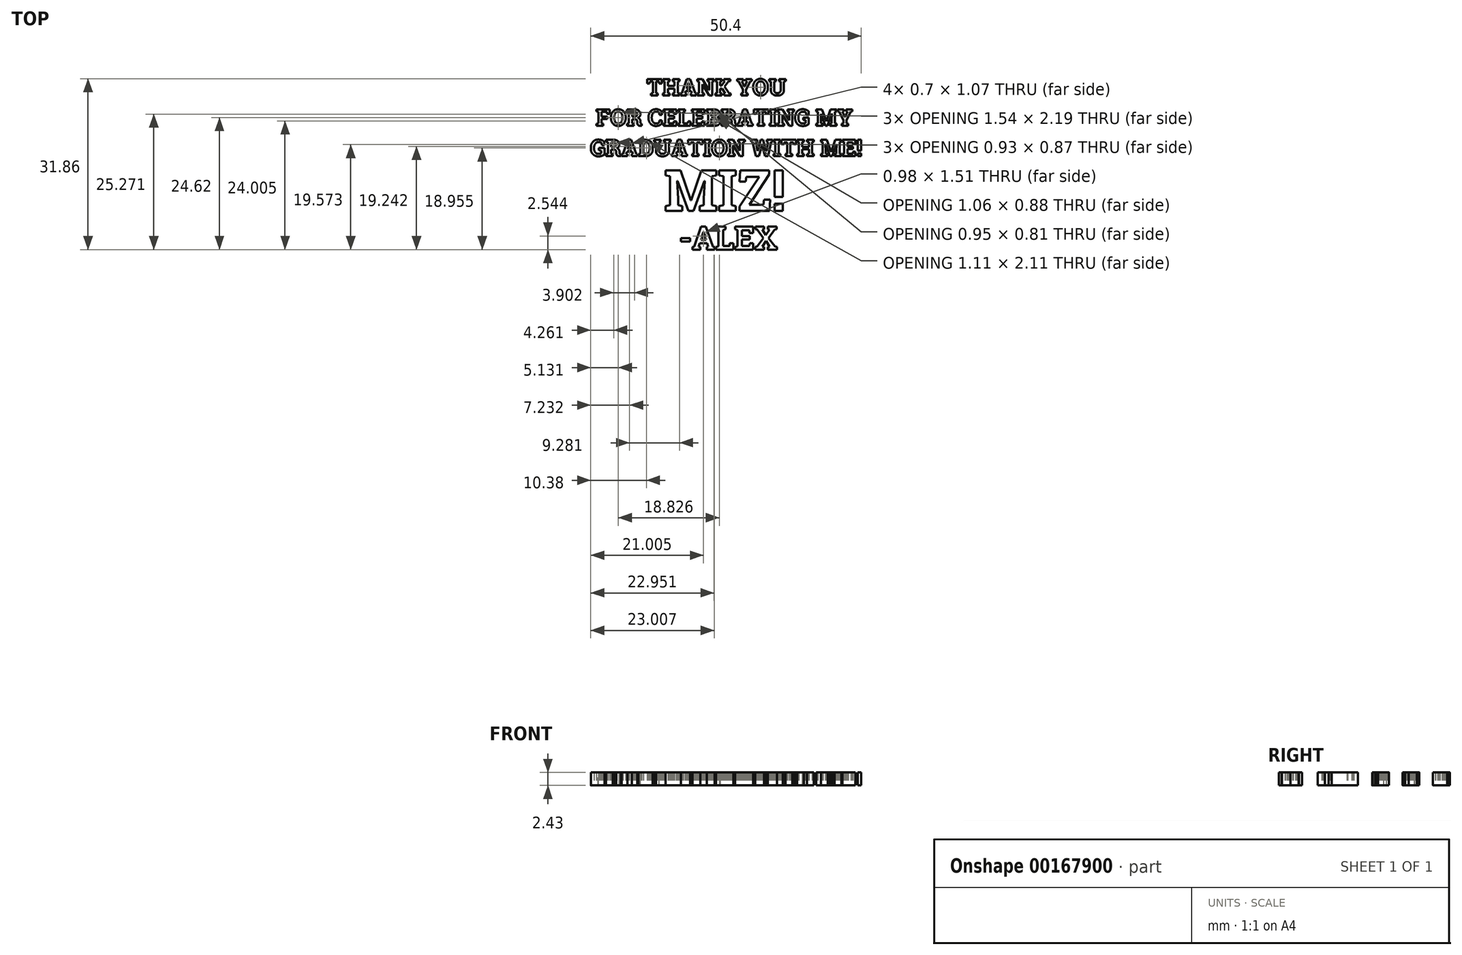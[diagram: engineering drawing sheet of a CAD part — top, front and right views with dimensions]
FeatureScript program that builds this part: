
annotation { "Feature Type Name" : "Feature", "Feature Type Description" : "" }
export const myFeature = defineFeature(function(context is Context, id is Id, definition is map)
    precondition{}
    {
        {
            var Q0;
            Q0=qCreatedBy(makeId("Top.planeOp"),FACE);
            var sketch = newSketch(context, id + "F0", { "sketchPlane" : qUnion([Q0])});
            skLineSegment(sketch, "E0.bottom", {"start": v(50.8, 50.8) * mm, "end": v(-50.8, 50.8) * mm});
            skLineSegment(sketch, "E0.top", {"start": v(50.8, -50.8) * mm, "end": v(-50.8, -50.8) * mm});
            skLineSegment(sketch, "E0.left", {"start": v(50.8, 50.8) * mm, "end": v(50.8, -50.8) * mm});
            skLineSegment(sketch, "E0.right", {"start": v(-50.8, 50.8) * mm, "end": v(-50.8, -50.8) * mm});
            skSolve(sketch);
        }
        {
            var Q0;
            Q0=makeQuery(id+"F0.imprint","IMPRINT",FACE,{"disambiguationData":[TD([[makeQuery(id+"F0.imprint","IMPRINT",EDGE,{"derivedFrom":sQuery(id+"F0.wireOp",EDGE,"E0.bottom")}),1.0]])]});
            extrude(context, id + "F1", {"entities" : qUnion([Q0]), "depth" : 0.25 * mm});
        }
        {
            var Q0;
            Q0=makeQuery(id+"F1.opExtrude","CAP_FACE",FACE,{"disambiguationData":[OSD([sQuery(id+"F0.wireOp",EDGE,"E0.bottom"),sQuery(id+"F0.wireOp",EDGE,"E0.top"),sQuery(id+"F0.wireOp",EDGE,"E0.left"),sQuery(id+"F0.wireOp",EDGE,"E0.right")])],"isStart":false});
            var sketch = newSketch(context, id + "F2", { "sketchPlane" : qUnion([Q0])});
            skPoint(sketch, "E1.middle", {"position": v(-1.1, 2.32) * mm});
            skArc(sketch, "E2", {"start": v(-32.91, -18.37) * mm, "mid": v(0.46, -46.42) * mm, "end": v(30.94, -15.26) * mm});
            skFitSpline(sketch, "E3", {"points": [v(9.59, 14.3) * mm, v(21.95, -4.32) * mm, v(30.83, -11.61) * mm], "startDerivative": vector(6.75, -28.22) * mm, "endDerivative": vector(20.93, -12.99) * mm});
            skArc(sketch, "E4.trimOffspring", {"start": v(-1.07, 17.65) * mm, "mid": v(-1.09, 17.65) * mm, "end": v(-1.1, 17.65) * mm});
            skFitSpline(sketch, "E5", {"points": [v(-33.16, -14.19) * mm, v(-18.4, -2.5) * mm, v(-11.4, 11.65) * mm, v(-1.07, 17.65) * mm, v(9.59, 14.3) * mm], "startDerivative": vector(61.53, 38.74) * mm, "endDerivative": vector(53, -36.24) * mm});
            skArc(sketch, "E6.filletArc", {"start": v(10.18, 12.44) * mm, "mid": v(9.06, 14.3) * mm, "end": v(7.37, 15.69) * mm});
            skArc(sketch, "E7.filletArc", {"start": v(-29.99, -12.2) * mm, "mid": v(-32.35, -14.86) * mm, "end": v(-32.91, -18.37) * mm});
            skArc(sketch, "E8.filletArc", {"start": v(30.94, -15.26) * mm, "mid": v(30.28, -12.26) * mm, "end": v(28.29, -9.93) * mm});
            skFitSpline(sketch, "E9", {"points": [v(-29.85, -3.68) * mm, v(-17.42, 9.03) * mm, v(-26.88, 28.6) * mm, v(-34.2, 34.36) * mm, v(-41.89, 25.81) * mm, v(-29.85, -3.68) * mm]});
            skFitSpline(sketch, "E10", {"points": [v(-9.26, 19.18) * mm, v(-1.93, 20.93) * mm, v(0, 34.01) * mm, v(-9.26, 49.2) * mm, v(-15.01, 43.26) * mm, v(-17.8, 31.57) * mm, v(-9.26, 19.18) * mm]});
            skFitSpline(sketch, "E11", {"points": [v(5.4, 19.88) * mm, v(5.75, 35.76) * mm, v(13.78, 48.15) * mm, v(20.06, 42.21) * mm, v(22.85, 29.65) * mm, v(15.7, 17.26) * mm, v(5.4, 19.88) * mm]});
            skFitSpline(sketch, "E12", {"points": [v(20.93, 6.1) * mm, v(27.74, -2.46) * mm, v(39.95, 4) * mm, v(45.88, 24.6) * mm, v(38.03, 34.19) * mm, v(26.7, 20.58) * mm, v(22.85, 12.55) * mm, v(20.93, 6.1) * mm]});
            skSolve(sketch);
        }
        {
            var Q0;
            Q0=makeQuery(id+"F2.imprint","IMPRINT",FACE,{"disambiguationData":[TD([[makeQuery(id+"F2.imprint","IMPRINT",EDGE,{"derivedFrom":sQuery(id+"F2.wireOp",EDGE,"E2")}),1.0]])]});
            var Q1;
            Q1=makeQuery(id+"F2.imprint","IMPRINT",FACE,{"disambiguationData":[TD([[makeQuery(id+"F2.imprint","IMPRINT",EDGE,{"derivedFrom":sQuery(id+"F2.wireOp",EDGE,"E10")}),1.0]])]});
            var Q2;
            Q2=makeQuery(id+"F2.imprint","IMPRINT",FACE,{"disambiguationData":[TD([[makeQuery(id+"F2.imprint","IMPRINT",EDGE,{"derivedFrom":sQuery(id+"F2.wireOp",EDGE,"E11")}),-1.0]])]});
            var Q3;
            Q3=makeQuery(id+"F2.imprint","IMPRINT",FACE,{"disambiguationData":[TD([[makeQuery(id+"F2.imprint","IMPRINT",EDGE,{"derivedFrom":sQuery(id+"F2.wireOp",EDGE,"E12")}),1.0]])]});
            var Q4;
            Q4=makeQuery(id+"F2.imprint","IMPRINT",FACE,{"disambiguationData":[TD([[makeQuery(id+"F2.imprint","IMPRINT",EDGE,{"derivedFrom":sQuery(id+"F2.wireOp",EDGE,"E9")}),1.0]])]});
            extrude(context, id + "F3", {"entities" : qUnion([Q0, Q1, Q2, Q3, Q4]), "operationType" : NewBodyOperationType.ADD, "depth" : 0.25 * mm});
        }
        {
            var Q0;
            Q0=makeQuery(id+"F3.opExtrude","CAP_EDGE",EDGE,{"disambiguationData":[OSD([sQuery(id+"F2.wireOp",EDGE,"E9")])],"isStart":false});
            fillet(context, id + "F4", {"entities" : qUnion([Q0]), "radius" : 1.9 * mm, "tangentPropagation" : true, "allowEdgeOverflow" : false});
        }
        {
            var Q0;
            Q0=makeQuery(id+"F3.opExtrude","CAP_EDGE",EDGE,{"disambiguationData":[OSD([sQuery(id+"F2.wireOp",EDGE,"E10")])],"isStart":false});
            fillet(context, id + "F5", {"entities" : qUnion([Q0]), "radius" : 1.9 * mm, "tangentPropagation" : true, "allowEdgeOverflow" : false});
        }
        {
            var Q0;
            Q0=makeQuery(id+"F3.opExtrude","CAP_EDGE",EDGE,{"disambiguationData":[OSD([sQuery(id+"F2.wireOp",EDGE,"E11")])],"isStart":false});
            fillet(context, id + "F6", {"entities" : qUnion([Q0]), "radius" : 1.9 * mm, "tangentPropagation" : true, "allowEdgeOverflow" : false});
        }
        {
            var Q0;
            Q0=makeQuery(id+"F3.opExtrude","CAP_EDGE",EDGE,{"disambiguationData":[OSD([sQuery(id+"F2.wireOp",EDGE,"E12")])],"isStart":false});
            fillet(context, id + "F7", {"entities" : qUnion([Q0]), "radius" : 1.9 * mm, "tangentPropagation" : true, "allowEdgeOverflow" : false});
        }
        {
            var Q0;
            Q0=makeQuery(id+"F3.opExtrude","CAP_EDGE",EDGE,{"disambiguationData":[OSD([sQuery(id+"F2.wireOp",EDGE,"E5")])],"isStart":false});
            fillet(context, id + "F8", {"entities" : qUnion([Q0]), "radius" : 1.9 * mm, "tangentPropagation" : true, "allowEdgeOverflow" : false});
        }
        {
            var Q0;
            Q0=makeQuery(id+"F1.opExtrude","CAP_EDGE",EDGE,{"disambiguationData":[OSD([sQuery(id+"F0.wireOp",EDGE,"E0.right")])],"isStart":false});
            fillet(context, id + "F9", {"entities" : qUnion([Q0]), "radius" : 1.27 * mm, "tangentPropagation" : true, "allowEdgeOverflow" : false});
        }
        {
            var Q0;
            Q0=makeQuery(id+"F1.opExtrude","CAP_EDGE",EDGE,{"disambiguationData":[OSD([sQuery(id+"F0.wireOp",EDGE,"E0.top")])],"isStart":false});
            fillet(context, id + "F10", {"entities" : qUnion([Q0]), "radius" : 1.27 * mm, "tangentPropagation" : true, "allowEdgeOverflow" : false});
        }
        {
            var Q0;
            Q0=makeQuery(id+"F1.opExtrude","CAP_EDGE",EDGE,{"disambiguationData":[OSD([sQuery(id+"F0.wireOp",EDGE,"E0.left")])],"isStart":false});
            fillet(context, id + "F11", {"entities" : qUnion([Q0]), "radius" : 1.27 * mm, "tangentPropagation" : true, "allowEdgeOverflow" : false});
        }
        {
            var Q0;
            Q0=makeQuery(id+"F1.opExtrude","CAP_EDGE",EDGE,{"disambiguationData":[OSD([sQuery(id+"F0.wireOp",EDGE,"E0.bottom")])],"isStart":false});
            fillet(context, id + "F12", {"entities" : qUnion([Q0]), "radius" : 1.27 * mm, "tangentPropagation" : true, "allowEdgeOverflow" : false});
        }
        {
            var Q0;
            Q0=makeQuery(id+"F3.opExtrude","CAP_FACE",FACE,{"disambiguationData":[OSD([sQuery(id+"F2.wireOp",EDGE,"E2"),sQuery(id+"F2.wireOp",EDGE,"E3"),sQuery(id+"F2.wireOp",EDGE,"E5"),sQuery(id+"F2.wireOp",EDGE,"E6.filletArc"),sQuery(id+"F2.wireOp",EDGE,"E7.filletArc"),sQuery(id+"F2.wireOp",EDGE,"E8.filletArc")])],"isStart":false});
            var sketch = newSketch(context, id + "F13", { "sketchPlane" : qUnion([Q0])});
            skText(sketch, "E13", { "text": "-ALEX", "fontName": "RobotoSlab-Bold.ttf"});
            skText(sketch, "E14", { "text": "                          THANK YOU \n                 FOR CELEBRATING MY \n                GRADUATION WITH ME!", "fontName": "RobotoSlab-Bold.ttf"});
            skText(sketch, "E15", { "text": "MIZ!", "fontName": "RobotoSlab-Bold.ttf"});
            const initialGuessF13  = {"E13": [-0.00867, -0.03756, 1, 0, 0.00434], "E14": [-0.04204, -0.0088, 1, 0, 0.00309], "E15": [-0.01144, -0.03033, 1, 0, 0.00762]};
            skSetInitialGuess(sketch, initialGuessF13);
            skSolve(sketch);
        }
        {
            var Q0;
            Q0 = qSketchRegion(id + "F13", true);
            extrude(context, id + "F14", {"entities" : qUnion([Q0]), "operationType" : NewBodyOperationType.ADD, "depth" : 5.2 * mm});
        }
        {
            var Q0;
            Q0=qCreatedBy(makeId("Right.planeOp"),FACE);
            var sketch = newSketch(context, id + "F15", { "sketchPlane" : qUnion([Q0])});
            skLineSegment(sketch, "E16.bottom", {"start": v(-50.86, 0.19) * mm, "end": v(51.2, 0.19) * mm});
            skLineSegment(sketch, "E16.top", {"start": v(-50.86, 3.3) * mm, "end": v(51.2, 3.3) * mm});
            skLineSegment(sketch, "E16.left", {"start": v(-50.86, 0.19) * mm, "end": v(-50.86, 3.3) * mm});
            skLineSegment(sketch, "E16.right", {"start": v(51.2, 0.19) * mm, "end": v(51.2, 3.3) * mm});
            skSolve(sketch);
        }
        {
            var Q0;
            Q0 = qSketchRegion(id + "F15", true);
            extrude(context, id + "F16", {"entities" : qUnion([Q0]), "operationType" : NewBodyOperationType.REMOVE, "endBound" : BoundingType.SYMMETRIC, "oppositeDirection" : true, "depth" : 101.6 * mm});
        }
        {
            var Q0;
            Q0=qCreatedBy(makeId("Right.planeOp"),FACE);
            var sketch = newSketch(context, id + "F17", { "sketchPlane" : qUnion([Q0])});
            skLineSegment(sketch, "E17.bottom", {"start": v(51.78, 0.9) * mm, "end": v(-51.78, 0.9) * mm});
            skLineSegment(sketch, "E17.top", {"start": v(51.78, -0.9) * mm, "end": v(-51.78, -0.9) * mm});
            skLineSegment(sketch, "E17.left", {"start": v(51.78, 0.9) * mm, "end": v(51.78, -0.9) * mm});
            skLineSegment(sketch, "E17.right", {"start": v(-51.78, 0.9) * mm, "end": v(-51.78, -0.9) * mm});
            skPoint(sketch, "E17.middle", {"position": v(0, 0) * mm});
            skSolve(sketch);
        }
        {
            var Q0;
            Q0 = qSketchRegion(id + "F17", true);
            extrude(context, id + "F18", {"entities" : qUnion([Q0]), "operationType" : NewBodyOperationType.REMOVE, "endBound" : BoundingType.SYMMETRIC, "oppositeDirection" : true, "depth" : 101.6 * mm});
        }
    });
